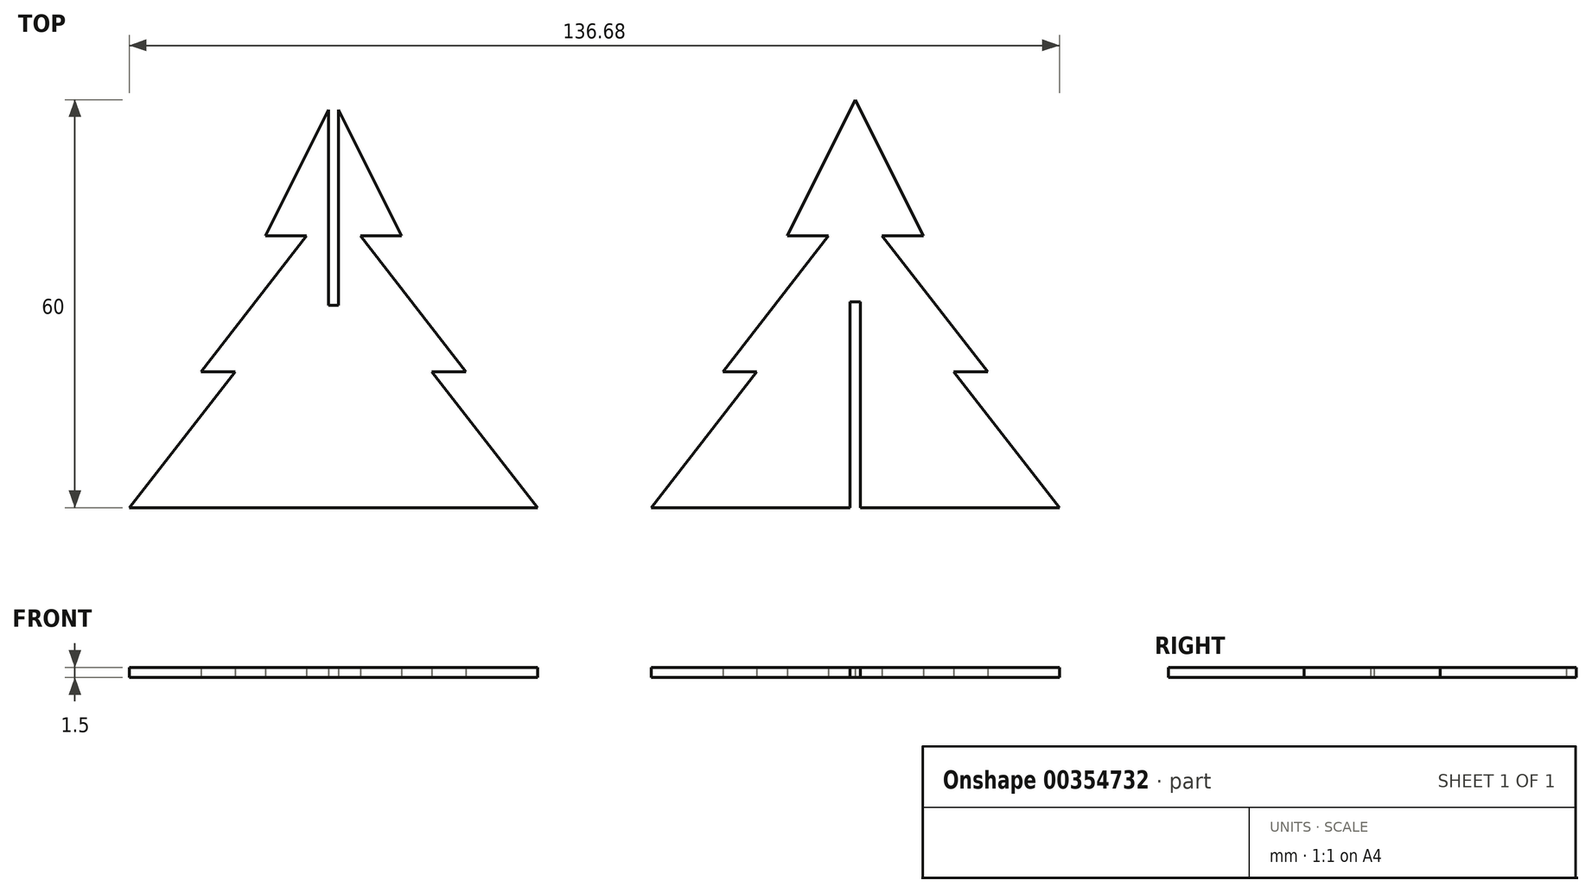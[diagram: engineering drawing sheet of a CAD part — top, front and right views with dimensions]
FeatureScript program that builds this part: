
annotation { "Feature Type Name" : "Feature", "Feature Type Description" : "" }
export const myFeature = defineFeature(function(context is Context, id is Id, definition is map)
    precondition{}
    {
        {
            var Q0;
            Q0=qCreatedBy(makeId("Top.planeOp"),FACE);
            var sketch = newSketch(context, id + "F0", { "sketchPlane" : qUnion([Q0])});
            skLineSegment(sketch, "E0", {"start": v(30, 0) * mm, "end": v(14.47, 20) * mm});
            skLineSegment(sketch, "E1", {"start": v(14.47, 20) * mm, "end": v(19.47, 20) * mm});
            skLineSegment(sketch, "E2", {"start": v(19.47, 20) * mm, "end": v(3.94, 40) * mm});
            skLineSegment(sketch, "E3", {"start": v(3.94, 40) * mm, "end": v(10, 40) * mm});
            skLineSegment(sketch, "E4", {"start": v(10, 40) * mm, "end": v(0, 60) * mm});
            skLineSegment(sketch, "E5.MirrorCS", {"start": v(-3.94, 40) * mm, "end": v(-10, 40) * mm});
            skLineSegment(sketch, "E6.MirrorCS", {"start": v(-19.47, 20) * mm, "end": v(-3.94, 40) * mm});
            skLineSegment(sketch, "E7.MirrorCS", {"start": v(-14.47, 20) * mm, "end": v(-19.47, 20) * mm});
            skLineSegment(sketch, "E8.MirrorCS", {"start": v(-30, 0) * mm, "end": v(-14.47, 20) * mm});
            skLineSegment(sketch, "E9.MirrorCS", {"start": v(-10, 40) * mm, "end": v(0, 60) * mm});
            skLineSegment(sketch, "E10", {"start": v(-38.34, 68.98) * mm, "end": v(-38.34, 0) * mm, "construction": true});
            skLineSegment(sketch, "E11.MirrorCS", {"start": v(-72.74, 40) * mm, "end": v(-66.68, 40) * mm});
            skLineSegment(sketch, "E12.MirrorCS", {"start": v(-80.63, 40) * mm, "end": v(-86.68, 40) * mm});
            skLineSegment(sketch, "E13.MirrorCS", {"start": v(-57.21, 20) * mm, "end": v(-72.74, 40) * mm});
            skLineSegment(sketch, "E14.MirrorCS", {"start": v(-96.15, 20) * mm, "end": v(-80.63, 40) * mm});
            skLineSegment(sketch, "E15.MirrorCS", {"start": v(-91.15, 20) * mm, "end": v(-96.15, 20) * mm});
            skLineSegment(sketch, "E16.MirrorCS", {"start": v(-106.68, 0) * mm, "end": v(-91.15, 20) * mm});
            skLineSegment(sketch, "E17.MirrorCS", {"start": v(-76.68, 0) * mm, "end": v(-106.68, 0) * mm});
            skLineSegment(sketch, "E18.MirrorCS", {"start": v(-76.68, 0) * mm, "end": v(-46.68, 0) * mm});
            skLineSegment(sketch, "E19.MirrorCS", {"start": v(-46.68, 0) * mm, "end": v(-62.21, 20) * mm});
            skLineSegment(sketch, "E20.MirrorCS", {"start": v(-62.21, 20) * mm, "end": v(-57.21, 20) * mm});
            skLineSegment(sketch, "E21", {"start": v(-75.93, 30) * mm, "end": v(-75.93, 58.5) * mm});
            skLineSegment(sketch, "E22.MirrorCS", {"start": v(-77.43, 30) * mm, "end": v(-77.43, 58.5) * mm});
            skLineSegment(sketch, "E23", {"start": v(-75.93, 58.5) * mm, "end": v(-66.68, 40) * mm});
            skLineSegment(sketch, "E24", {"start": v(-77.43, 58.5) * mm, "end": v(-86.68, 40) * mm});
            skLineSegment(sketch, "E25", {"start": v(0.75, 0) * mm, "end": v(30, 0) * mm});
            skLineSegment(sketch, "E26", {"start": v(-0.75, 0) * mm, "end": v(-30, 0) * mm});
            skLineSegment(sketch, "E27", {"start": v(0, 60) * mm, "end": v(0, 0) * mm, "construction": true});
            skLineSegment(sketch, "E28.MirrorCS", {"start": v(-76.68, 60) * mm, "end": v(-76.68, 0) * mm, "construction": true});
            skLineSegment(sketch, "E29", {"start": v(0, 60) * mm, "end": v(0, 30) * mm, "construction": true});
            skLineSegment(sketch, "E30", {"start": v(-0.75, 0) * mm, "end": v(-0.75, 30.25) * mm});
            skLineSegment(sketch, "E31", {"start": v(-0.75, 30.25) * mm, "end": v(0.75, 30.25) * mm});
            skLineSegment(sketch, "E32.MirrorCS", {"start": v(0.75, 0) * mm, "end": v(0.75, 30.25) * mm});
            skLineSegment(sketch, "E33", {"start": v(-75.93, 30) * mm, "end": v(-75.93, 29.75) * mm});
            skLineSegment(sketch, "E34.MirrorCS", {"start": v(-77.43, 30) * mm, "end": v(-77.43, 29.75) * mm});
            skLineSegment(sketch, "E35", {"start": v(-77.43, 29.75) * mm, "end": v(-75.93, 29.75) * mm});
            skSolve(sketch);
        }
        {
            var Q0;
            Q0=makeQuery(id+"F0.imprint","IMPRINT",FACE,{"disambiguationData":[TD([[makeQuery(id+"F0.imprint","IMPRINT",EDGE,{"derivedFrom":sQuery(id+"F0.wireOp",EDGE,"E11.MirrorCS")}),1.0]])]});
            var Q1;
            Q1=makeQuery(id+"F0.imprint","IMPRINT",FACE,{"disambiguationData":[TD([[makeQuery(id+"F0.imprint","IMPRINT",EDGE,{"derivedFrom":sQuery(id+"F0.wireOp",EDGE,"E0")}),1.0]])]});
            extrude(context, id + "F1", {"entities" : qUnion([Q0, Q1]), "depth" : 1.5 * mm});
        }
    });
